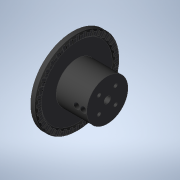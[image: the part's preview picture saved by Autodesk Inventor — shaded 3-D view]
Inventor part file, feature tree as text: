
AUTODESK INVENTOR PART (.ipt)
format: ipt  version: 2021 (Build 250183000, 183)  size: 376,320 bytes
history: native  units: mm
features: extrude x5, sketch x5, projected_geometry x3, revolve x1, plane x1, pattern_circular x1
ambient origin geometry x8: Origin, YZ Plane, XZ Plane, XY Plane, X Axis, Y Axis, Z Axis, Center Point
bodies: Solid1 (feature_tree)
feature tree (16):
  revolve  "Revolution1"  [1 undecoded]
  extrude  "Extrusion1"  Depth=16.0mm
  plane  "Work Plane1"
  extrude  "Extrusion2"  Depth=2.0mm
  extrude  "Extrusion3"  Depth=45.0mm
  pattern_circular  "Circular Pattern1"  [2 undecoded]
  sketch  "Sketch5"  dims[d8=25.0mm d9=5.0mm d10=4.0mm d11=90.0deg d12=2.8mm d13=30.0mm d14=8.0mm d15=0.0mm d16=0.0mm d17=30.0mm d18=7.5mm d19=12.0mm d20=0.0mm d21=1.0mm d22=1.0mm d23=3.0mm d25=1.0mm d26=0.0mm d27=0.0mm d28=360.0mm d29=360.0deg d31=20.0mm d32=20.0mm d33=10.0mm d34=10.0mm d35=4.2mm d36=6.2mm d37=0.0mm d38=3.2mm d39=0.0mm d40=0.0mm]
  extrude  "Extrusion4"  Depth=4.0mm
  extrude  "Extrusion5"  TaperAngle=90.0deg  [1 undecoded]
  sketch  "Sketch1"  dims[d0=4.0mm d1=19.0mm]
  sketch  "Sketch2"  dims[d2=26.0mm d3=16.0mm]
  sketch  "Sketch3"  dims[d4=2.0mm d5=2.0mm]
  projected_geometry  "Projected Loop3"
  projected_geometry  "Projected Loop4"
  sketch  "Sketch4"  dims[d6=2.0mm d7=45.0mm]
  projected_geometry  "Projected Loop5"
note: 4 required parameter values undecoded (feature->parameter linkage not recoverable at this tier; creation-order binding heuristic only, values carry confidence <= 0.55)